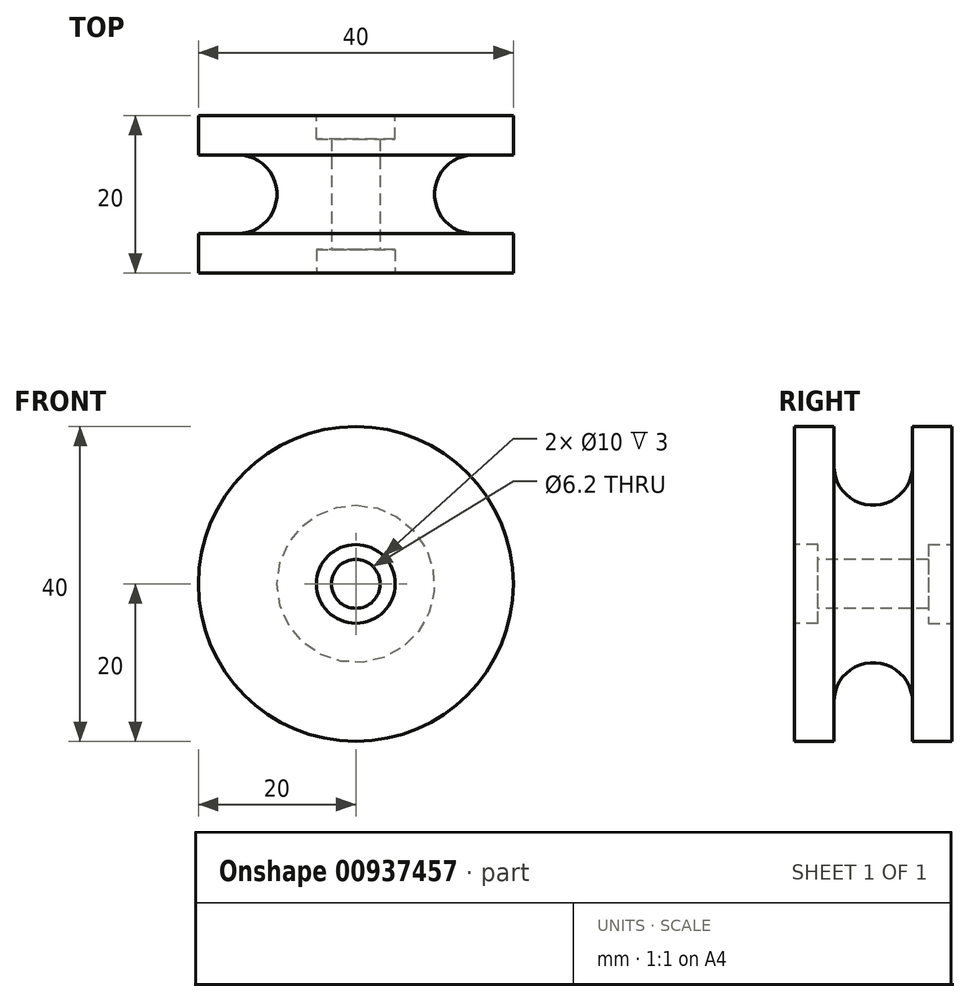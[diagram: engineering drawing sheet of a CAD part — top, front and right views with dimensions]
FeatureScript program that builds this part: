
annotation { "Feature Type Name" : "Feature", "Feature Type Description" : "" }
export const myFeature = defineFeature(function(context is Context, id is Id, definition is map)
    precondition{}
    {
        {
            var Q0;
            Q0=qCreatedBy(makeId("Front.planeOp"),FACE);
            var sketch = newSketch(context, id + "F0", { "sketchPlane" : qUnion([Q0])});
            skCircle(sketch, "E0", {"center": v(0, 0) * mm, "radius": 15 * mm});
            skSolve(sketch);
        }
        {
            var Q0;
            Q0=makeQuery(id+"F0.imprint","IMPRINT",FACE,{"disambiguationData":[TD([[makeQuery(id+"F0.imprint","IMPRINT",EDGE,{"derivedFrom":sQuery(id+"F0.wireOp",EDGE,"E0")}),1.0]])]});
            extrude(context, id + "F1", {"entities" : qUnion([Q0]), "depth" : 5 * mm, "offsetDistance" : 25 * mm});
        }
        {
            var Q0;
            Q0=makeQuery(id+"F1.opExtrude","CAP_FACE",FACE,{"disambiguationData":[OSD([sQuery(id+"F0.wireOp",EDGE,"E0")])],"isStart":true});
            var sketch = newSketch(context, id + "F2", { "sketchPlane" : qUnion([Q0])});
            skCircle(sketch, "E1", {"center": v(0, 0) * mm, "radius": 15 * mm});
            skSolve(sketch);
        }
        {
            var Q0;
            Q0=makeQuery(id+"F2.imprint","IMPRINT",FACE,{"disambiguationData":[TD([[makeQuery(id+"F2.imprint","IMPRINT",EDGE,{"derivedFrom":sQuery(id+"F2.wireOp",EDGE,"E1")}),-1.0]])]});
            extrude(context, id + "F3", {"entities" : qUnion([Q0]), "operationType" : NewBodyOperationType.ADD, "depth" : 5 * mm, "offsetDistance" : 25 * mm});
        }
        {
            var Q0;
            Q0=qCreatedBy(makeId("Right.planeOp"),FACE);
            var sketch = newSketch(context, id + "F4", { "sketchPlane" : qUnion([Q0])});
            skCircle(sketch, "E2", {"center": v(0, -15) * mm, "radius": 5 * mm});
            skSolve(sketch);
        }
        {
            var Q0;
            Q0 = qSketchRegion(id + "F4", true);
            var Q1;
            Q1 = qConstructionFilter(qBodyType(qCreatedBy(id + "F2" ,EDGE), BodyType.WIRE), ConstructionObject.NO);
            sweep(context, id + "F5", {"operationType" : NewBodyOperationType.REMOVE, "profiles" : qUnion([Q0]), "path" : qUnion([Q1])});
        }
        {
            var Q0;
            Q0=makeQuery(id+"F1.opExtrude","CAP_FACE",FACE,{"disambiguationData":[OSD([sQuery(id+"F0.wireOp",EDGE,"E0")])],"isStart":false});
            var sketch = newSketch(context, id + "F6", { "sketchPlane" : qUnion([Q0])});
            skCircle(sketch, "E3", {"center": v(0, 0) * mm, "radius": 20 * mm});
            skSolve(sketch);
        }
        {
            var Q0;
            Q0 = qSketchRegion(id + "F6", true);
            extrude(context, id + "F7", {"entities" : qUnion([Q0]), "operationType" : NewBodyOperationType.ADD, "depth" : 5 * mm, "offsetDistance" : 25 * mm});
        }
        {
            var Q0;
            Q0=makeQuery(id+"F3.opExtrude","CAP_FACE",FACE,{"disambiguationData":[OSD([sQuery(id+"F2.wireOp",EDGE,"E1")])],"isStart":false});
            var sketch = newSketch(context, id + "F8", { "sketchPlane" : qUnion([Q0])});
            skCircle(sketch, "E4", {"center": v(0, 0) * mm, "radius": 20 * mm});
            skSolve(sketch);
        }
        {
            var Q0;
            Q0 = qSketchRegion(id + "F8", true);
            extrude(context, id + "F9", {"entities" : qUnion([Q0]), "operationType" : NewBodyOperationType.ADD, "depth" : 5 * mm, "offsetDistance" : 25 * mm});
        }
        {
            var Q0;
            Q0=makeQuery(id+"F7.opExtrude","CAP_FACE",FACE,{"disambiguationData":[OSD([sQuery(id+"F6.wireOp",EDGE,"E3")])],"isStart":false});
            var sketch = newSketch(context, id + "F10", { "sketchPlane" : qUnion([Q0])});
            skCircle(sketch, "E5", {"center": v(0, 0) * mm, "radius": 3.1 * mm});
            skCircle(sketch, "E6", {"center": v(0, 0) * mm, "radius": 5 * mm});
            skSolve(sketch);
        }
        {
            var Q0;
            Q0=makeQuery(id+"F10.imprint","IMPRINT",FACE,{"disambiguationData":[TD([[makeQuery(id+"F10.imprint","IMPRINT",EDGE,{"derivedFrom":sQuery(id+"F10.wireOp",EDGE,"E5")}),1.0]])]});
            extrude(context, id + "F11", {"entities" : qUnion([Q0]), "operationType" : NewBodyOperationType.REMOVE, "oppositeDirection" : true, "depth" : 25 * mm, "offsetDistance" : 25 * mm});
        }
        {
            var Q0;
            Q0=makeQuery(id+"F10.imprint","IMPRINT",FACE,{"disambiguationData":[TD([[makeQuery(id+"F10.imprint","IMPRINT",EDGE,{"derivedFrom":sQuery(id+"F10.wireOp",EDGE,"E5")}),-1.0]])]});
            extrude(context, id + "F12", {"entities" : qUnion([Q0]), "operationType" : NewBodyOperationType.REMOVE, "oppositeDirection" : true, "depth" : 3 * mm, "offsetDistance" : 25 * mm});
        }
        {
            var Q0;
            Q0=makeQuery(id+"F9.opExtrude","CAP_FACE",FACE,{"disambiguationData":[OSD([sQuery(id+"F8.wireOp",EDGE,"E4")])],"isStart":false});
            var sketch = newSketch(context, id + "F13", { "sketchPlane" : qUnion([Q0])});
            skCircle(sketch, "E7", {"center": v(0, 0) * mm, "radius": 5 * mm});
            skSolve(sketch);
        }
        {
            var Q0;
            Q0=makeQuery(id+"F13.imprint","IMPRINT",FACE,{"disambiguationData":[TD([[makeQuery(id+"F13.imprint","IMPRINT",EDGE,{"derivedFrom":sQuery(id+"F13.wireOp",EDGE,"E7")}),1.0]])]});
            extrude(context, id + "F14", {"entities" : qUnion([Q0]), "operationType" : NewBodyOperationType.REMOVE, "oppositeDirection" : true, "depth" : 3 * mm, "offsetDistance" : 25 * mm});
        }
    });
